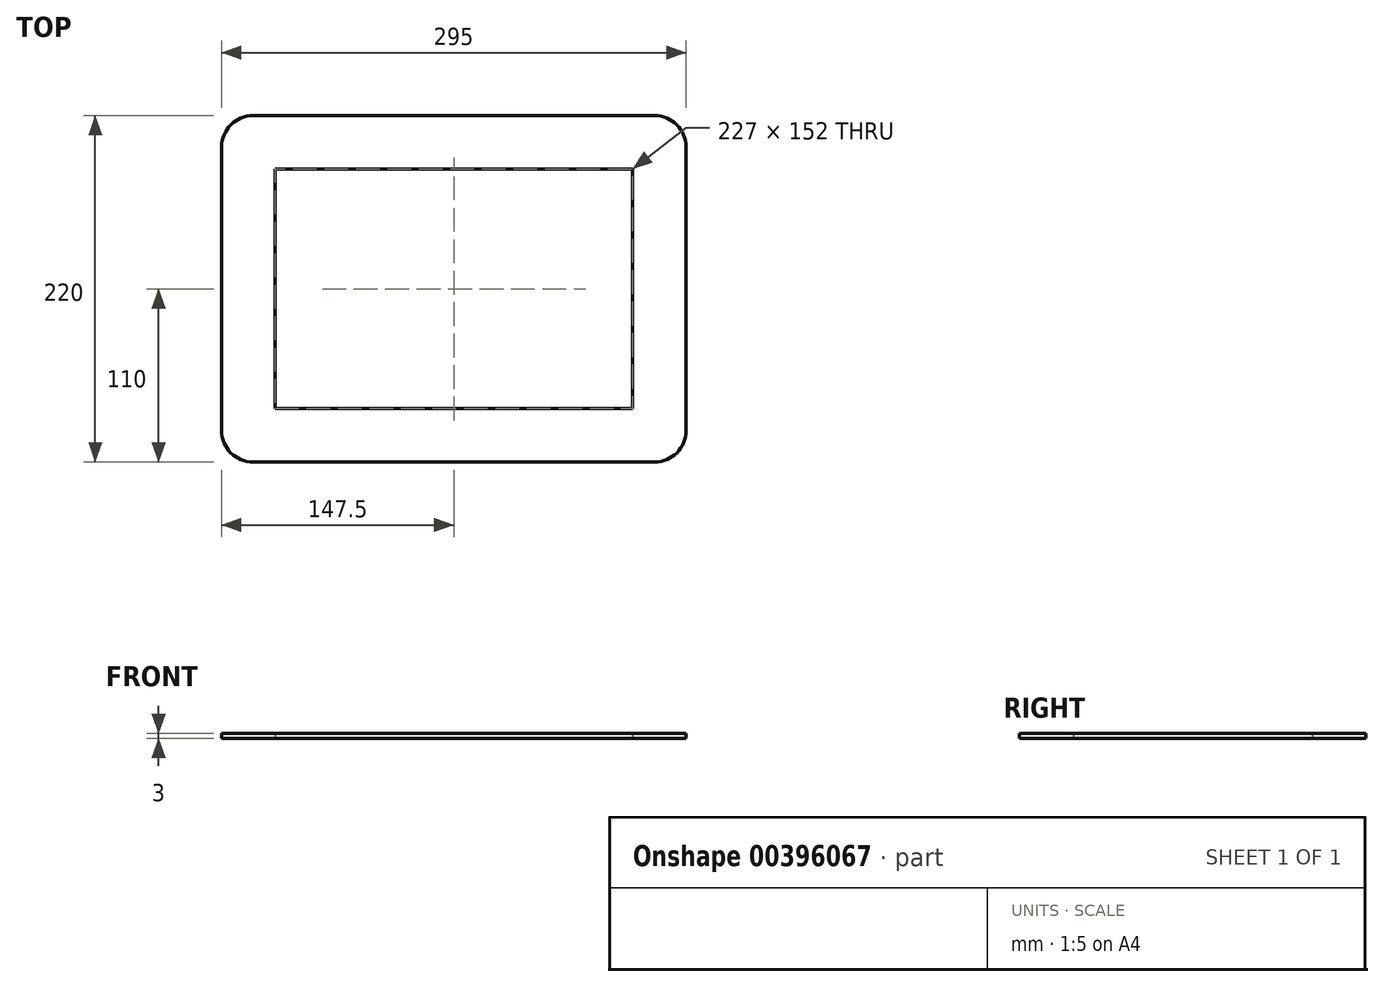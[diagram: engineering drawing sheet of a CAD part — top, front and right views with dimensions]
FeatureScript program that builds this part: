
annotation { "Feature Type Name" : "Feature", "Feature Type Description" : "" }
export const myFeature = defineFeature(function(context is Context, id is Id, definition is map)
    precondition{}
    {
        {
            var Q0;
            Q0=qCreatedBy(makeId("Top.planeOp"),FACE);
            var sketch = newSketch(context, id + "F0", { "sketchPlane" : qUnion([Q0])});
            skLineSegment(sketch, "E0.bottom", {"start": v(-127.5, 110) * mm, "end": v(127.5, 110) * mm});
            skLineSegment(sketch, "E0.top", {"start": v(-127.5, -110) * mm, "end": v(127.5, -110) * mm});
            skLineSegment(sketch, "E0.left", {"start": v(-147.5, 90) * mm, "end": v(-147.5, -90) * mm});
            skLineSegment(sketch, "E0.right", {"start": v(147.5, 90) * mm, "end": v(147.5, -90) * mm});
            skPoint(sketch, "E0.middle", {"position": v(0, 0) * mm});
            skPoint(sketch, "E1.visualSharp", {"position": v(-147.5, 110) * mm});
            skArc(sketch, "E1.filletArc", {"start": v(-127.5, 110) * mm, "mid": v(-141.64, 104.14) * mm, "end": v(-147.5, 90) * mm});
            skPoint(sketch, "E2.visualSharp", {"position": v(-147.5, -110) * mm});
            skArc(sketch, "E2.filletArc", {"start": v(-147.5, -90) * mm, "mid": v(-141.64, -104.14) * mm, "end": v(-127.5, -110) * mm});
            skPoint(sketch, "E3.visualSharp", {"position": v(147.5, -110) * mm});
            skArc(sketch, "E3.filletArc", {"start": v(127.5, -110) * mm, "mid": v(141.64, -104.14) * mm, "end": v(147.5, -90) * mm});
            skPoint(sketch, "E4.visualSharp", {"position": v(147.5, 110) * mm});
            skArc(sketch, "E4.filletArc", {"start": v(147.5, 90) * mm, "mid": v(141.64, 104.14) * mm, "end": v(127.5, 110) * mm});
            skLineSegment(sketch, "E5.bottom", {"start": v(-113.5, 76) * mm, "end": v(113.5, 76) * mm});
            skLineSegment(sketch, "E5.top", {"start": v(-113.5, -76) * mm, "end": v(113.5, -76) * mm});
            skLineSegment(sketch, "E5.left", {"start": v(-113.5, 76) * mm, "end": v(-113.5, -76) * mm});
            skLineSegment(sketch, "E5.right", {"start": v(113.5, 76) * mm, "end": v(113.5, -76) * mm});
            skSolve(sketch);
        }
        {
            var Q0;
            Q0=qSketchRegion(id+"F0",true);
            extrude(context, id + "F1", {"entities" : qUnion([Q0]), "depth" : 3 * mm});
        }
    });
